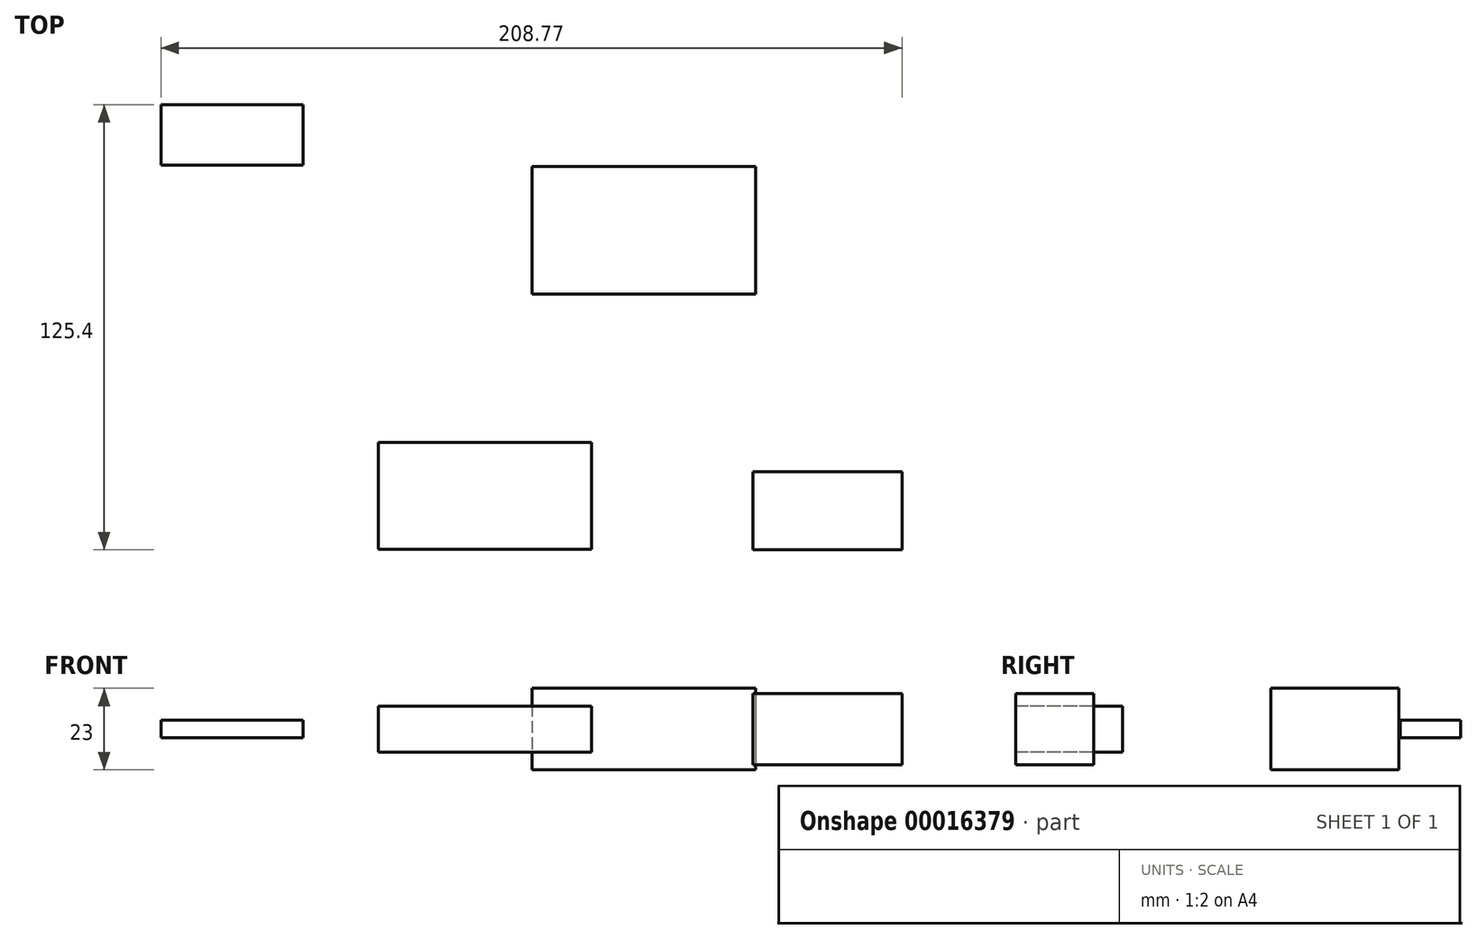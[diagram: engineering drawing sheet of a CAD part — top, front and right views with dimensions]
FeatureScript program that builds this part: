
annotation { "Feature Type Name" : "Feature", "Feature Type Description" : "" }
export const myFeature = defineFeature(function(context is Context, id is Id, definition is map)
    precondition{}
    {
        {
            var Q0;
            Q0=qCreatedBy(makeId("Top.planeOp"),FACE);
            var sketch = newSketch(context, id + "F0", { "sketchPlane" : qUnion([Q0])});
            skLineSegment(sketch, "E0.bottom", {"start": v(-28.2, 26.9) * mm, "end": v(34.8, 26.9) * mm});
            skLineSegment(sketch, "E0.top", {"start": v(-28.2, -9.1) * mm, "end": v(34.8, -9.1) * mm});
            skLineSegment(sketch, "E0.left", {"start": v(-28.2, 26.9) * mm, "end": v(-28.2, -9.1) * mm});
            skLineSegment(sketch, "E0.right", {"start": v(34.8, 26.9) * mm, "end": v(34.8, -9.1) * mm});
            skSolve(sketch);
        }
        {
            var Q0;
            Q0 = qSketchRegion(id + "F0", true);
            extrude(context, id + "F1", {"entities" : qUnion([Q0]), "endBound" : BoundingType.SYMMETRIC, "depth" : 23 * mm});
        }
        {
            var Q0;
            Q0=qCreatedBy(makeId("Top.planeOp"),FACE);
            var sketch = newSketch(context, id + "F2", { "sketchPlane" : qUnion([Q0])});
            skLineSegment(sketch, "E1.bottom", {"start": v(-71.46, -50.9) * mm, "end": v(-11.46, -50.9) * mm});
            skLineSegment(sketch, "E1.top", {"start": v(-71.46, -80.9) * mm, "end": v(-11.46, -80.9) * mm});
            skLineSegment(sketch, "E1.left", {"start": v(-71.46, -50.9) * mm, "end": v(-71.46, -80.9) * mm});
            skLineSegment(sketch, "E1.right", {"start": v(-11.46, -50.9) * mm, "end": v(-11.46, -80.9) * mm});
            skSolve(sketch);
        }
        {
            var Q0;
            Q0 = qSketchRegion(id + "F2", true);
            extrude(context, id + "F3", {"entities" : qUnion([Q0]), "endBound" : BoundingType.SYMMETRIC, "depth" : 13 * mm});
        }
        {
            var Q0;
            Q0=qCreatedBy(makeId("Top.planeOp"),FACE);
            var sketch = newSketch(context, id + "F4", { "sketchPlane" : qUnion([Q0])});
            skLineSegment(sketch, "E2.bottom", {"start": v(-132.76, 44.3) * mm, "end": v(-92.76, 44.3) * mm});
            skLineSegment(sketch, "E2.top", {"start": v(-132.76, 27.3) * mm, "end": v(-92.76, 27.3) * mm});
            skLineSegment(sketch, "E2.left", {"start": v(-132.76, 44.3) * mm, "end": v(-132.76, 27.3) * mm});
            skLineSegment(sketch, "E2.right", {"start": v(-92.76, 44.3) * mm, "end": v(-92.76, 27.3) * mm});
            skSolve(sketch);
        }
        {
            var Q0;
            Q0 = qSketchRegion(id + "F4", true);
            extrude(context, id + "F5", {"entities" : qUnion([Q0]), "endBound" : BoundingType.SYMMETRIC, "depth" : 5 * mm});
        }
        {
            var Q0;
            Q0=qCreatedBy(makeId("Top.planeOp"),FACE);
            var sketch = newSketch(context, id + "F6", { "sketchPlane" : qUnion([Q0])});
            skLineSegment(sketch, "E3.bottom", {"start": v(34.01, -59.1) * mm, "end": v(76.01, -59.1) * mm});
            skLineSegment(sketch, "E3.top", {"start": v(34.01, -81.1) * mm, "end": v(76.01, -81.1) * mm});
            skLineSegment(sketch, "E3.left", {"start": v(34.01, -59.1) * mm, "end": v(34.01, -81.1) * mm});
            skLineSegment(sketch, "E3.right", {"start": v(76.01, -59.1) * mm, "end": v(76.01, -81.1) * mm});
            skSolve(sketch);
        }
        {
            var Q0;
            Q0 = qSketchRegion(id + "F6", true);
            extrude(context, id + "F7", {"entities" : qUnion([Q0]), "endBound" : BoundingType.SYMMETRIC, "depth" : 20 * mm});
        }
    });
